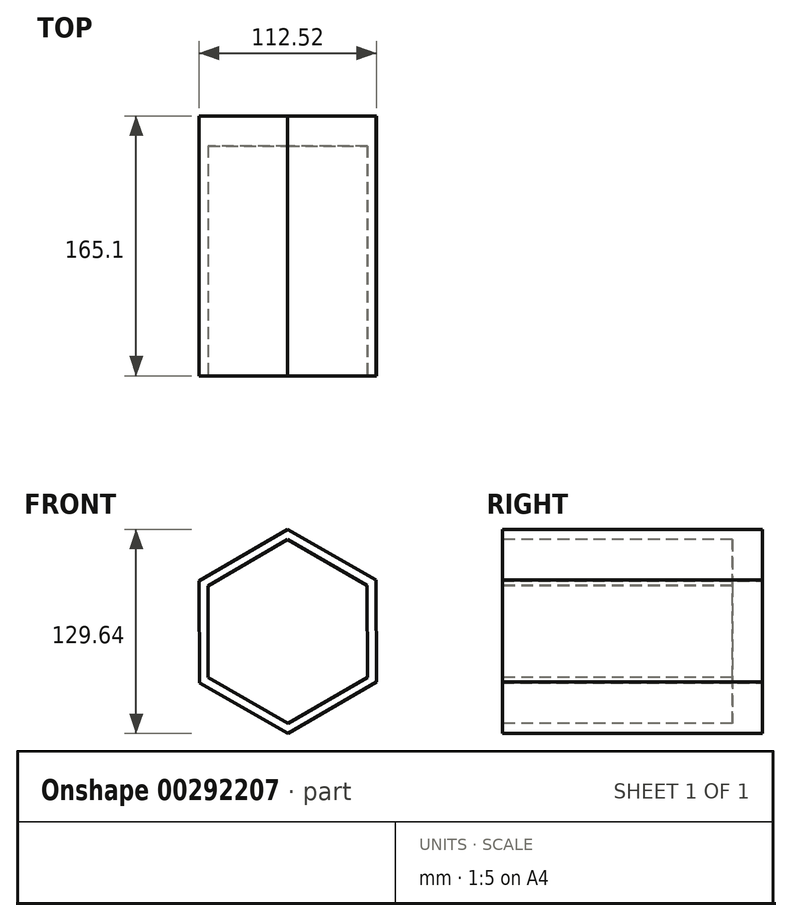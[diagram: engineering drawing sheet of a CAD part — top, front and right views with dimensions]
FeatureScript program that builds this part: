
annotation { "Feature Type Name" : "Feature", "Feature Type Description" : "" }
export const myFeature = defineFeature(function(context is Context, id is Id, definition is map)
    precondition{}
    {
        {
            var Q0;
            Q0=qCreatedBy(makeId("Front.planeOp"),FACE);
            var sketch = newSketch(context, id + "F0", { "sketchPlane" : qUnion([Q0])});
            skCircle(sketch, "E0.cCircle", {"center": v(0, 0) * mm, "radius": 56.14 * mm, "construction": true});
            skLineSegment(sketch, "E0.0", {"start": v(-56.26, 32.19) * mm, "end": v(-0.26, 64.82) * mm});
            skLineSegment(sketch, "E0.1", {"start": v(-0.26, 64.82) * mm, "end": v(56, 32.63) * mm});
            skLineSegment(sketch, "E0.2", {"start": v(56, 32.63) * mm, "end": v(56.26, -32.19) * mm});
            skLineSegment(sketch, "E0.3", {"start": v(56.26, -32.19) * mm, "end": v(0.26, -64.82) * mm});
            skLineSegment(sketch, "E0.4", {"start": v(0.26, -64.82) * mm, "end": v(-56, -32.63) * mm});
            skLineSegment(sketch, "E0.5", {"start": v(-56, -32.63) * mm, "end": v(-56.26, 32.19) * mm});
            skPoint(sketch, "E0.0.midPoint", {"position": v(-28.26, 48.5) * mm});
            skSolve(sketch);
        }
        {
            var Q0;
            Q0 = qSketchRegion(id + "F0", true);
            extrude(context, id + "F1", {"entities" : qUnion([Q0]), "depth" : 165.1 * mm});
        }
        {
            var Q0;
            Q0 = qSketchRegion(id + "F0", true);
            var Q1;
            Q1 = qSketchRegion(id + "F29AD1Np9tiicVI_1", true);
            extrude(context, id + "F2", {"entities" : qUnion([Q0, Q1]), "operationType" : NewBodyOperationType.ADD, "depth" : 127 * mm});
        }
        {
            var Q0;
            Q0=makeQuery(id+"F1.opExtrude","CAP_FACE",FACE,{"disambiguationData":[OSD([sQuery(id+"F0.wireOp",EDGE,"E0.0"),sQuery(id+"F0.wireOp",EDGE,"E0.1"),sQuery(id+"F0.wireOp",EDGE,"E0.2"),sQuery(id+"F0.wireOp",EDGE,"E0.3"),sQuery(id+"F0.wireOp",EDGE,"E0.4"),sQuery(id+"F0.wireOp",EDGE,"E0.5")])],"isStart":false});
            var sketch = newSketch(context, id + "F3", { "sketchPlane" : qUnion([Q0])});
            skCircle(sketch, "E1.cCircle", {"center": v(0, 0) * mm, "radius": 50.57 * mm, "construction": true});
            skLineSegment(sketch, "E1.0", {"start": v(-50.64, 29.07) * mm, "end": v(-0.15, 58.4) * mm});
            skLineSegment(sketch, "E1.1", {"start": v(-0.15, 58.4) * mm, "end": v(50.5, 29.33) * mm});
            skLineSegment(sketch, "E1.2", {"start": v(50.5, 29.33) * mm, "end": v(50.64, -29.07) * mm});
            skLineSegment(sketch, "E1.3", {"start": v(50.64, -29.07) * mm, "end": v(0.15, -58.4) * mm});
            skLineSegment(sketch, "E1.4", {"start": v(0.15, -58.4) * mm, "end": v(-50.5, -29.33) * mm});
            skLineSegment(sketch, "E1.5", {"start": v(-50.5, -29.33) * mm, "end": v(-50.64, 29.07) * mm});
            skPoint(sketch, "E1.0.midPoint", {"position": v(-25.4, 43.73) * mm});
            skSolve(sketch);
        }
        {
            var Q0;
            Q0 = qSketchRegion(id + "F3", true);
            extrude(context, id + "F4", {"entities" : qUnion([Q0]), "operationType" : NewBodyOperationType.REMOVE, "oppositeDirection" : true, "depth" : 146.05 * mm});
        }
    });
